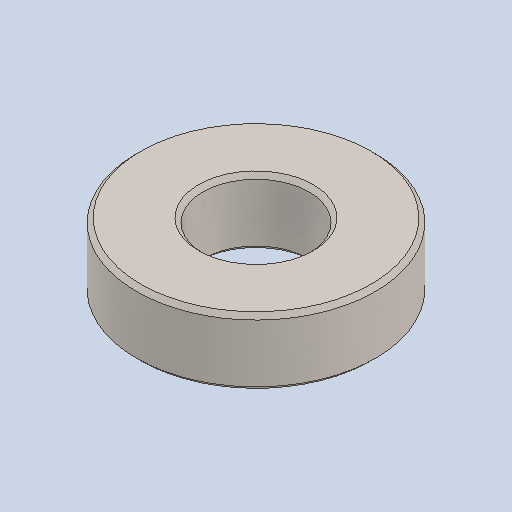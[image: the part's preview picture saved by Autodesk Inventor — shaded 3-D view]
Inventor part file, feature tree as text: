
AUTODESK INVENTOR PART (.ipt)
format: ipt  version: 2024.2 (Build 282272000, 272)  size: 103,424 bytes
history: native  units: in
note: dims shown in document units (in); Inventor stores cm internally (conversion verified against a paired STEP export)
features: chamfer x1
ambient origin geometry x8: Origin, YZ Plane, XZ Plane, XY Plane, X Axis, Y Axis, Z Axis, Center Point
bodies: Solid1 (feature_tree)
feature tree (1):
  chamfer  "Chamfer1"  [1 undecoded]
note: 1 required parameter value undecoded (feature->parameter linkage not recoverable at this tier; creation-order binding heuristic only, values carry confidence <= 0.55)
